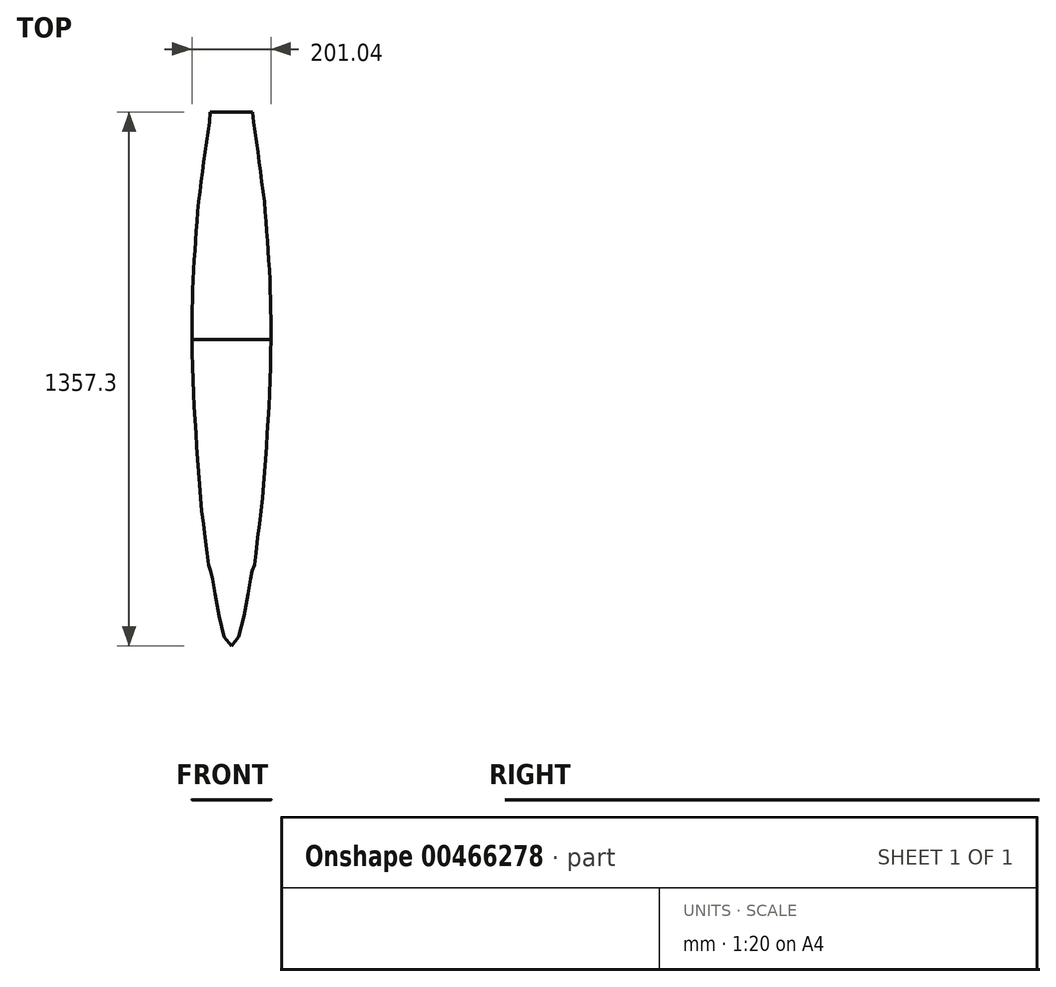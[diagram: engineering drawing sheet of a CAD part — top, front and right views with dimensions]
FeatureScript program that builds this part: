
annotation { "Feature Type Name" : "Feature", "Feature Type Description" : "" }
export const myFeature = defineFeature(function(context is Context, id is Id, definition is map)
    precondition{}
    {
        {
            var Q0;
            Q0=qCreatedBy(makeId("Front.planeOp"),FACE);
            cPlane(context, id + "F0", {"entities" : qUnion([Q0]), "cplaneType" : CPlaneType.OFFSET, "offset" : 76.2 * mm, "width" : 152.4 * mm, "height" : 152.4 * mm});
        }
        {
            var Q0;
            Q0=qCreatedBy(makeId("Front.planeOp"),FACE);
            cPlane(context, id + "F1", {"entities" : qUnion([Q0]), "cplaneType" : CPlaneType.OFFSET, "offset" : 149.22 * mm, "width" : 152.4 * mm, "height" : 152.4 * mm});
        }
        {
            var Q0;
            Q0=qCreatedBy(makeId("Front.planeOp"),FACE);
            cPlane(context, id + "F2", {"entities" : qUnion([Q0]), "cplaneType" : CPlaneType.OFFSET, "offset" : 223.85 * mm, "width" : 152.4 * mm, "height" : 152.4 * mm});
        }
        {
            var Q0;
            Q0=qCreatedBy(makeId("Front.planeOp"),FACE);
            cPlane(context, id + "F3", {"entities" : qUnion([Q0]), "cplaneType" : CPlaneType.OFFSET, "offset" : 296.88 * mm, "width" : 152.4 * mm, "height" : 152.4 * mm});
        }
        {
            var Q0;
            Q0=qCreatedBy(makeId("Front.planeOp"),FACE);
            cPlane(context, id + "F4", {"entities" : qUnion([Q0]), "cplaneType" : CPlaneType.OFFSET, "offset" : 371.47 * mm, "width" : 152.4 * mm, "height" : 152.4 * mm});
        }
        {
            var Q0;
            Q0=qCreatedBy(makeId("Front.planeOp"),FACE);
            cPlane(context, id + "F5", {"entities" : qUnion([Q0]), "cplaneType" : CPlaneType.OFFSET, "offset" : 444.5 * mm, "width" : 152.4 * mm, "height" : 152.4 * mm});
        }
        {
            var Q0;
            Q0=qCreatedBy(makeId("Front.planeOp"),FACE);
            cPlane(context, id + "F6", {"entities" : qUnion([Q0]), "cplaneType" : CPlaneType.OFFSET, "offset" : 517.52 * mm, "width" : 152.4 * mm, "height" : 152.4 * mm});
        }
        {
            var Q0;
            Q0=qCreatedBy(makeId("Front.planeOp"),FACE);
            cPlane(context, id + "F7", {"entities" : qUnion([Q0]), "cplaneType" : CPlaneType.OFFSET, "offset" : 590.55 * mm, "width" : 152.4 * mm, "height" : 152.4 * mm});
        }
        {
            var Q0;
            Q0=qCreatedBy(makeId("Front.planeOp"),FACE);
            cPlane(context, id + "F8", {"entities" : qUnion([Q0]), "cplaneType" : CPlaneType.OFFSET, "offset" : 658.83 * mm, "width" : 152.4 * mm, "height" : 152.4 * mm});
        }
        {
            var Q0;
            Q0=qCreatedBy(makeId("Front.planeOp"),FACE);
            cPlane(context, id + "F9", {"entities" : qUnion([Q0]), "cplaneType" : CPlaneType.OFFSET, "offset" : 730.25 * mm, "width" : 152.4 * mm, "height" : 152.4 * mm});
        }
        {
            var Q0;
            Q0=qCreatedBy(makeId("Front.planeOp"),FACE);
            cPlane(context, id + "F10", {"entities" : qUnion([Q0]), "cplaneType" : CPlaneType.OFFSET, "offset" : 801.7 * mm, "width" : 152.4 * mm, "height" : 152.4 * mm});
        }
        {
            var Q0;
            Q0=qCreatedBy(makeId("Front.planeOp"),FACE);
            cPlane(context, id + "F11", {"entities" : qUnion([Q0]), "cplaneType" : CPlaneType.OFFSET, "offset" : 874.73 * mm, "width" : 152.4 * mm, "height" : 152.4 * mm});
        }
        {
            var Q0;
            Q0=qCreatedBy(makeId("Front.planeOp"),FACE);
            cPlane(context, id + "F12", {"entities" : qUnion([Q0]), "cplaneType" : CPlaneType.OFFSET, "offset" : 949.32 * mm, "width" : 152.4 * mm, "height" : 152.4 * mm});
        }
        {
            var Q0;
            Q0=qCreatedBy(makeId("Front.planeOp"),FACE);
            cPlane(context, id + "F13", {"entities" : qUnion([Q0]), "cplaneType" : CPlaneType.OFFSET, "offset" : 1023.95 * mm, "width" : 152.4 * mm, "height" : 152.4 * mm});
        }
        {
            var Q0;
            Q0=qCreatedBy(makeId("Front.planeOp"),FACE);
            cPlane(context, id + "F14", {"entities" : qUnion([Q0]), "cplaneType" : CPlaneType.OFFSET, "offset" : 1096.98 * mm, "width" : 152.4 * mm, "height" : 152.4 * mm});
        }
        {
            var Q0;
            Q0=qCreatedBy(makeId("Front.planeOp"),FACE);
            cPlane(context, id + "F15", {"entities" : qUnion([Q0]), "cplaneType" : CPlaneType.OFFSET, "offset" : 1168.4 * mm, "width" : 152.4 * mm, "height" : 152.4 * mm});
        }
        {
            var Q0;
            Q0=qCreatedBy(makeId("Front.planeOp"),FACE);
            cPlane(context, id + "F16", {"entities" : qUnion([Q0]), "cplaneType" : CPlaneType.OFFSET, "offset" : 1233.5 * mm, "width" : 152.4 * mm, "height" : 152.4 * mm});
        }
        {
            var Q0;
            Q0=qCreatedBy(makeId("Front.planeOp"),FACE);
            cPlane(context, id + "F17", {"entities" : qUnion([Q0]), "cplaneType" : CPlaneType.OFFSET, "offset" : 1304.92 * mm, "width" : 152.4 * mm, "height" : 152.4 * mm});
        }
        {
            var Q0;
            Q0=qCreatedBy(makeId("Front.planeOp"),FACE);
            cPlane(context, id + "F18", {"entities" : qUnion([Q0]), "cplaneType" : CPlaneType.OFFSET, "offset" : 1377.95 * mm, "width" : 152.4 * mm, "height" : 152.4 * mm});
        }
        {
            var Q0;
            Q0=qCreatedBy(makeId("Front.planeOp"),FACE);
            cPlane(context, id + "F19", {"entities" : qUnion([Q0]), "cplaneType" : CPlaneType.OFFSET, "offset" : 1450.97 * mm, "width" : 152.4 * mm, "height" : 152.4 * mm});
        }
        {
            var Q0;
            Q0=qCreatedBy(makeId("Front.planeOp"),FACE);
            cPlane(context, id + "F20", {"entities" : qUnion([Q0]), "cplaneType" : CPlaneType.OFFSET, "offset" : 1524 * mm, "width" : 152.4 * mm, "height" : 152.4 * mm});
        }
        {
            var Q0;
            Q0=qCreatedBy(id+"F0.planeOp",FACE);
            var sketch = newSketch(context, id + "F21", { "sketchPlane" : qUnion([Q0])});
            skPoint(sketch, "E0", {"position": v(0, 45.6) * mm});
            skPoint(sketch, "E1", {"position": v(3.3, 99.95) * mm});
            skPoint(sketch, "E2", {"position": v(6.35, 110.5) * mm});
            skPoint(sketch, "E3", {"position": v(9.52, 114.5) * mm});
            skPoint(sketch, "E4", {"position": v(12.7, 116.71) * mm});
            skFitSpline(sketch, "E5", {"points": [v(12.7, 116.71) * mm, v(9.53, 114.5) * mm, v(6.35, 110.5) * mm, v(3.3, 99.95) * mm, v(0, 45.6) * mm], "startDerivative": vector(-25.87, -11.48) * mm, "endDerivative": vector(-23.07, -0.86) * mm});
            skFitSpline(sketch, "E6.MirrorCS", {"points": [v(-12.7, 116.71) * mm, v(-9.53, 114.5) * mm, v(-6.35, 110.5) * mm, v(-3.3, 99.95) * mm, v(0, 45.6) * mm], "startDerivative": vector(25.87, -11.48) * mm, "endDerivative": vector(23.07, -0.86) * mm});
            skSolve(sketch);
        }
        {
            var Q0;
            Q0=qCreatedBy(id+"F1.planeOp",FACE);
            var sketch = newSketch(context, id + "F22", { "sketchPlane" : qUnion([Q0])});
            skPoint(sketch, "E7", {"position": v(0, 3.56) * mm});
            skPoint(sketch, "E8", {"position": v(3.18, 4.45) * mm});
            skPoint(sketch, "E9", {"position": v(6.35, 14.99) * mm});
            skPoint(sketch, "E10", {"position": v(9.53, 28.96) * mm});
            skPoint(sketch, "E11", {"position": v(12.7, 55) * mm});
            skPoint(sketch, "E12", {"position": v(15.88, 72.77) * mm});
            skPoint(sketch, "E13", {"position": v(19.05, 83.06) * mm});
            skPoint(sketch, "E14", {"position": v(22.23, 92.58) * mm});
            skPoint(sketch, "E15", {"position": v(25.4, 99.7) * mm});
            skPoint(sketch, "E16", {"position": v(28.58, 105.16) * mm});
            skPoint(sketch, "E17", {"position": v(31.75, 109.7) * mm});
            skPoint(sketch, "E18", {"position": v(34.93, 114.43) * mm});
            skFitSpline(sketch, "E19", {"points": [v(34.93, 114.43) * mm, v(31.75, 109.7) * mm, v(28.58, 105.16) * mm, v(25.4, 99.7) * mm, v(22.23, 92.58) * mm, v(19.05, 83.06) * mm, v(15.88, 72.77) * mm, v(12.7, 55) * mm, v(9.53, 28.96) * mm, v(6.35, 14.99) * mm, v(3.18, 4.45) * mm, v(0, 3.56) * mm], "startDerivative": vector(-45.98, -69.77) * mm, "endDerivative": vector(-66.01, 0.7) * mm});
            skFitSpline(sketch, "E20.MirrorCS", {"points": [v(-34.93, 114.43) * mm, v(-31.75, 109.7) * mm, v(-28.58, 105.16) * mm, v(-25.4, 99.7) * mm, v(-22.23, 92.58) * mm, v(-19.05, 83.06) * mm, v(-15.88, 72.77) * mm, v(-12.7, 55) * mm, v(-9.53, 28.96) * mm, v(-6.35, 14.99) * mm, v(-3.18, 4.45) * mm, v(0, 3.56) * mm], "startDerivative": vector(45.98, -69.77) * mm, "endDerivative": vector(66.01, 0.7) * mm});
            skSolve(sketch);
        }
        {
            var Q0;
            Q0=qCreatedBy(id+"F2.planeOp",FACE);
            var sketch = newSketch(context, id + "F23", { "sketchPlane" : qUnion([Q0])});
            skPoint(sketch, "E21", {"position": v(0, 0) * mm});
            skPoint(sketch, "E22", {"position": v(3.18, 0.89) * mm});
            skPoint(sketch, "E23", {"position": v(6.35, 5.59) * mm});
            skPoint(sketch, "E24", {"position": v(9.53, 10.03) * mm});
            skPoint(sketch, "E25", {"position": v(12.7, 15.88) * mm});
            skPoint(sketch, "E26", {"position": v(15.88, 21.9) * mm});
            skPoint(sketch, "E27", {"position": v(19.05, 29.46) * mm});
            skPoint(sketch, "E28", {"position": v(22.23, 37.97) * mm});
            skPoint(sketch, "E29", {"position": v(25.4, 51.94) * mm});
            skPoint(sketch, "E30", {"position": v(28.58, 65.66) * mm});
            skPoint(sketch, "E31", {"position": v(31.75, 75.06) * mm});
            skPoint(sketch, "E32", {"position": v(34.93, 81.4) * mm});
            skPoint(sketch, "E33", {"position": v(38.1, 88.27) * mm});
            skPoint(sketch, "E34", {"position": v(41.28, 95.96) * mm});
            skPoint(sketch, "E35", {"position": v(44.45, 101.73) * mm});
            skPoint(sketch, "E36", {"position": v(47.63, 106.3) * mm});
            skPoint(sketch, "E37", {"position": v(50.8, 111.46) * mm});
            skFitSpline(sketch, "E38", {"points": [v(50.8, 111.46) * mm, v(47.63, 106.3) * mm, v(44.45, 101.73) * mm, v(41.28, 95.96) * mm, v(38.1, 88.27) * mm, v(34.93, 81.4) * mm, v(31.75, 75.06) * mm, v(28.58, 65.66) * mm, v(25.4, 51.94) * mm, v(22.23, 37.97) * mm, v(19.05, 29.46) * mm, v(15.88, 21.9) * mm, v(12.7, 15.88) * mm, v(9.53, 10.03) * mm, v(6.35, 5.59) * mm, v(3.18, 0.89) * mm, v(0, 0) * mm], "startDerivative": vector(-55.85, -94.62) * mm, "endDerivative": vector(-81.33, -5.78) * mm});
            skFitSpline(sketch, "E39.MirrorCS", {"points": [v(-50.8, 111.46) * mm, v(-47.63, 106.3) * mm, v(-44.45, 101.73) * mm, v(-41.28, 95.96) * mm, v(-38.1, 88.27) * mm, v(-34.93, 81.4) * mm, v(-31.75, 75.06) * mm, v(-28.58, 65.66) * mm, v(-25.4, 51.94) * mm, v(-22.23, 37.97) * mm, v(-19.05, 29.46) * mm, v(-15.88, 21.9) * mm, v(-12.7, 15.88) * mm, v(-9.53, 10.03) * mm, v(-6.35, 5.59) * mm, v(-3.18, 0.89) * mm, v(0, 0) * mm], "startDerivative": vector(55.85, -94.62) * mm, "endDerivative": vector(81.33, -5.78) * mm});
            skSolve(sketch);
        }
        {
            var Q0;
            Q0=qCreatedBy(id+"F3.planeOp",FACE);
            var sketch = newSketch(context, id + "F24", { "sketchPlane" : qUnion([Q0])});
            skPoint(sketch, "E40", {"position": v(0, 0) * mm});
            skPoint(sketch, "E41", {"position": v(3.18, 0) * mm});
            skPoint(sketch, "E42", {"position": v(6.35, 1.78) * mm});
            skPoint(sketch, "E43", {"position": v(9.53, 4.57) * mm});
            skPoint(sketch, "E44", {"position": v(12.7, 7.06) * mm});
            skPoint(sketch, "E45", {"position": v(15.88, 9.9) * mm});
            skPoint(sketch, "E46", {"position": v(19.05, 12.83) * mm});
            skPoint(sketch, "E47", {"position": v(22.23, 16.26) * mm});
            skPoint(sketch, "E48", {"position": v(25.4, 19.81) * mm});
            skPoint(sketch, "E49", {"position": v(28.58, 24.38) * mm});
            skPoint(sketch, "E50", {"position": v(31.75, 29.46) * mm});
            skPoint(sketch, "E51", {"position": v(34.93, 35.56) * mm});
            skPoint(sketch, "E52", {"position": v(38.1, 44.45) * mm});
            skPoint(sketch, "E53", {"position": v(41.28, 53.72) * mm});
            skPoint(sketch, "E54", {"position": v(44.45, 67.1) * mm});
            skPoint(sketch, "E55", {"position": v(47.63, 78.36) * mm});
            skPoint(sketch, "E56", {"position": v(50.8, 86.74) * mm});
            skPoint(sketch, "E57", {"position": v(52.07, 88.9) * mm});
            skPoint(sketch, "E58", {"position": v(53.98, 93.05) * mm});
            skFitSpline(sketch, "E59", {"points": [v(53.98, 93.05) * mm, v(52.07, 88.9) * mm, v(50.8, 86.74) * mm, v(47.63, 78.36) * mm, v(44.45, 67.1) * mm, v(41.28, 53.72) * mm, v(38.1, 44.45) * mm, v(34.93, 35.56) * mm, v(31.75, 29.46) * mm, v(28.58, 24.38) * mm, v(25.4, 19.81) * mm, v(22.23, 16.26) * mm, v(19.05, 12.83) * mm, v(15.88, 9.9) * mm, v(12.7, 7.06) * mm, v(9.53, 4.57) * mm, v(6.35, 1.78) * mm, v(3.18, 0) * mm, v(0, 0) * mm], "startDerivative": vector(0, -48.17) * mm, "endDerivative": vector(-83.73, 12.68) * mm});
            skFitSpline(sketch, "E60.MirrorCS", {"points": [v(-53.98, 93.05) * mm, v(-52.07, 88.9) * mm, v(-50.8, 86.74) * mm, v(-47.63, 78.36) * mm, v(-44.45, 67.1) * mm, v(-41.28, 53.72) * mm, v(-38.1, 44.45) * mm, v(-34.93, 35.56) * mm, v(-31.75, 29.46) * mm, v(-28.58, 24.38) * mm, v(-25.4, 19.81) * mm, v(-22.23, 16.26) * mm, v(-19.05, 12.83) * mm, v(-15.88, 9.9) * mm, v(-12.7, 7.06) * mm, v(-9.53, 4.57) * mm, v(-6.35, 1.78) * mm, v(-3.18, 0) * mm, v(0, 0) * mm], "startDerivative": vector(0, -48.17) * mm, "endDerivative": vector(83.73, 12.68) * mm});
            skSolve(sketch);
        }
        {
            var Q0;
            Q0=qCreatedBy(id+"F4.planeOp",FACE);
            var sketch = newSketch(context, id + "F25", { "sketchPlane" : qUnion([Q0])});
            skPoint(sketch, "E61", {"position": v(0, 0) * mm});
            skPoint(sketch, "E62", {"position": v(6.35, 1.52) * mm});
            skPoint(sketch, "E63", {"position": v(12.7, 3.3) * mm});
            skPoint(sketch, "E64", {"position": v(19.05, 6.22) * mm});
            skPoint(sketch, "E65", {"position": v(25.4, 9.14) * mm});
            skPoint(sketch, "E66", {"position": v(31.75, 13.46) * mm});
            skPoint(sketch, "E67", {"position": v(38.1, 18.16) * mm});
            skPoint(sketch, "E68", {"position": v(44.45, 25.27) * mm});
            skPoint(sketch, "E69", {"position": v(50.8, 35.05) * mm});
            skPoint(sketch, "E70", {"position": v(53.98, 40.39) * mm});
            skPoint(sketch, "E71", {"position": v(57.15, 48.26) * mm});
            skPoint(sketch, "E72", {"position": v(60.33, 58.42) * mm});
            skPoint(sketch, "E73", {"position": v(63.5, 72.64) * mm});
            skPoint(sketch, "E74", {"position": v(60.33, 74.42) * mm});
            skPoint(sketch, "E75", {"position": v(63.5, 93.22) * mm});
            skFitSpline(sketch, "E76", {"points": [v(63.5, 93.22) * mm, v(60.33, 74.42) * mm, v(63.5, 72.64) * mm, v(60.33, 58.42) * mm, v(57.15, 48.26) * mm, v(53.98, 40.39) * mm, v(50.8, 35.05) * mm, v(44.45, 25.27) * mm, v(38.1, 18.16) * mm, v(31.75, 13.46) * mm, v(25.4, 9.14) * mm, v(19.05, 6.22) * mm, v(12.7, 3.3) * mm, v(6.35, 1.52) * mm, v(0, 0) * mm], "startDerivative": vector(-79.19, -170.03) * mm, "endDerivative": vector(-100.93, -19.54) * mm});
            skFitSpline(sketch, "E77.MirrorCS", {"points": [v(-63.5, 93.22) * mm, v(-60.33, 74.42) * mm, v(-63.5, 72.64) * mm, v(-60.33, 58.42) * mm, v(-57.15, 48.26) * mm, v(-53.98, 40.39) * mm, v(-50.8, 35.05) * mm, v(-44.45, 25.27) * mm, v(-38.1, 18.16) * mm, v(-31.75, 13.46) * mm, v(-25.4, 9.14) * mm, v(-19.05, 6.22) * mm, v(-12.7, 3.3) * mm, v(-6.35, 1.52) * mm, v(0, 0) * mm], "startDerivative": vector(79.19, -170.03) * mm, "endDerivative": vector(100.93, -19.54) * mm});
            skSolve(sketch);
        }
        {
            var Q0;
            Q0=qCreatedBy(id+"F5.planeOp",FACE);
            var sketch = newSketch(context, id + "F26", { "sketchPlane" : qUnion([Q0])});
            skPoint(sketch, "E78", {"position": v(0, 0) * mm});
            skPoint(sketch, "E79", {"position": v(6.35, 1.27) * mm});
            skPoint(sketch, "E80", {"position": v(12.7, 2.03) * mm});
            skPoint(sketch, "E81", {"position": v(19.05, 3.81) * mm});
            skPoint(sketch, "E82", {"position": v(25.4, 4.83) * mm});
            skPoint(sketch, "E83", {"position": v(31.75, 6.48) * mm});
            skPoint(sketch, "E84", {"position": v(38.1, 7.87) * mm});
            skPoint(sketch, "E85", {"position": v(44.45, 9.65) * mm});
            skPoint(sketch, "E86", {"position": v(50.8, 12.45) * mm});
            skPoint(sketch, "E87", {"position": v(57.15, 17.27) * mm});
            skPoint(sketch, "E88", {"position": v(60.33, 21.2) * mm});
            skPoint(sketch, "E89", {"position": v(63.5, 25.4) * mm});
            skPoint(sketch, "E90", {"position": v(66.68, 30.86) * mm});
            skPoint(sketch, "E91", {"position": v(69.85, 37.85) * mm});
            skPoint(sketch, "E92", {"position": v(73.03, 47) * mm});
            skPoint(sketch, "E93", {"position": v(76.2, 60.05) * mm});
            skPoint(sketch, "E94", {"position": v(77.8, 71.88) * mm});
            skPoint(sketch, "E95", {"position": v(73.03, 73.91) * mm});
            skPoint(sketch, "E96", {"position": v(73.03, 93.22) * mm});
            skFitSpline(sketch, "E97", {"points": [v(73.03, 93.22) * mm, v(73.03, 73.91) * mm, v(77.8, 71.88) * mm, v(76.2, 60.05) * mm, v(73.03, 47) * mm, v(69.85, 37.85) * mm, v(66.68, 30.86) * mm, v(63.5, 25.4) * mm, v(60.33, 21.2) * mm, v(57.15, 17.27) * mm, v(50.8, 12.45) * mm, v(44.45, 9.65) * mm, v(38.1, 7.87) * mm, v(31.75, 6.48) * mm, v(25.4, 4.83) * mm, v(19.05, 3.81) * mm, v(12.7, 2.03) * mm, v(6.35, 1.27) * mm, v(0, 0) * mm], "startDerivative": vector(-44, -271.62) * mm, "endDerivative": vector(-123.94, -29.25) * mm});
            skFitSpline(sketch, "E98.MirrorCS", {"points": [v(-73.03, 93.22) * mm, v(-73.03, 73.91) * mm, v(-77.8, 71.88) * mm, v(-76.2, 60.05) * mm, v(-73.03, 47) * mm, v(-69.85, 37.85) * mm, v(-66.68, 30.86) * mm, v(-63.5, 25.4) * mm, v(-60.33, 21.2) * mm, v(-57.15, 17.27) * mm, v(-50.8, 12.45) * mm, v(-44.45, 9.65) * mm, v(-38.1, 7.87) * mm, v(-31.75, 6.48) * mm, v(-25.4, 4.83) * mm, v(-19.05, 3.81) * mm, v(-12.7, 2.03) * mm, v(-6.35, 1.27) * mm, v(0, 0) * mm], "startDerivative": vector(44, -271.62) * mm, "endDerivative": vector(123.94, -29.25) * mm});
            skSolve(sketch);
        }
        {
            var Q0;
            Q0=qCreatedBy(id+"F6.planeOp",FACE);
            var sketch = newSketch(context, id + "F27", { "sketchPlane" : qUnion([Q0])});
            skPoint(sketch, "E99", {"position": v(0, 0) * mm});
            skPoint(sketch, "E100", {"position": v(19.05, 0) * mm});
            skPoint(sketch, "E101", {"position": v(25.4, 0.5) * mm});
            skPoint(sketch, "E102", {"position": v(31.75, 1.27) * mm});
            skPoint(sketch, "E103", {"position": v(38.1, 2.29) * mm});
            skPoint(sketch, "E104", {"position": v(44.45, 3.3) * mm});
            skPoint(sketch, "E105", {"position": v(50.8, 4.57) * mm});
            skPoint(sketch, "E106", {"position": v(56.96, 6.48) * mm});
            skPoint(sketch, "E107", {"position": v(63.5, 8.64) * mm});
            skPoint(sketch, "E108", {"position": v(69.85, 11.43) * mm});
            skPoint(sketch, "E109", {"position": v(73.03, 14.22) * mm});
            skPoint(sketch, "E110", {"position": v(76.2, 18.29) * mm});
            skPoint(sketch, "E111", {"position": v(79.38, 22.86) * mm});
            skPoint(sketch, "E112", {"position": v(82.55, 29.21) * mm});
            skPoint(sketch, "E113", {"position": v(86.36, 47) * mm});
            skPoint(sketch, "E114", {"position": v(87.33, 72.14) * mm});
            skPoint(sketch, "E115", {"position": v(84.15, 74.68) * mm});
            skPoint(sketch, "E116", {"position": v(82.55, 93.22) * mm});
            skFitSpline(sketch, "E117", {"points": [v(82.55, 93.22) * mm, v(84.15, 74.68) * mm, v(87.33, 72.14) * mm, v(86.36, 47) * mm, v(82.55, 29.21) * mm, v(79.38, 22.86) * mm, v(76.2, 18.29) * mm, v(73.03, 14.22) * mm, v(69.85, 11.43) * mm, v(63.5, 8.64) * mm, v(56.96, 6.48) * mm, v(50.8, 4.57) * mm, v(44.45, 3.3) * mm, v(38.1, 2.29) * mm, v(31.75, 1.27) * mm, v(25.4, 0.5) * mm, v(19.05, 0) * mm, v(0, 0) * mm], "startDerivative": vector(-5.3, -256.42) * mm, "endDerivative": vector(-246.88, 8.43) * mm});
            skFitSpline(sketch, "E118.MirrorCS", {"points": [v(-82.55, 93.22) * mm, v(-84.15, 74.68) * mm, v(-87.33, 72.14) * mm, v(-86.36, 47) * mm, v(-82.55, 29.21) * mm, v(-79.38, 22.86) * mm, v(-76.2, 18.29) * mm, v(-73.03, 14.22) * mm, v(-69.85, 11.43) * mm, v(-63.5, 8.64) * mm, v(-56.96, 6.48) * mm, v(-50.8, 4.57) * mm, v(-44.45, 3.3) * mm, v(-38.1, 2.29) * mm, v(-31.75, 1.27) * mm, v(-25.4, 0.5) * mm, v(-19.05, 0) * mm, v(0, 0) * mm], "startDerivative": vector(5.3, -256.42) * mm, "endDerivative": vector(246.88, 8.43) * mm});
            skSolve(sketch);
        }
        {
            var Q0;
            Q0=qCreatedBy(id+"F7.planeOp",FACE);
            var sketch = newSketch(context, id + "F28", { "sketchPlane" : qUnion([Q0])});
            skPoint(sketch, "E119", {"position": v(31.75, 0) * mm});
            skPoint(sketch, "E120", {"position": v(38.1, 0.5) * mm});
            skPoint(sketch, "E121", {"position": v(44.45, 1.02) * mm});
            skPoint(sketch, "E122", {"position": v(50.8, 1.52) * mm});
            skPoint(sketch, "E123", {"position": v(57.15, 2.03) * mm});
            skPoint(sketch, "E124", {"position": v(63.5, 2.67) * mm});
            skPoint(sketch, "E125", {"position": v(69.85, 3.05) * mm});
            skPoint(sketch, "E126", {"position": v(76.2, 3.81) * mm});
            skPoint(sketch, "E127", {"position": v(79.38, 4.57) * mm});
            skPoint(sketch, "E128", {"position": v(82.55, 6.35) * mm});
            skPoint(sketch, "E129", {"position": v(85.73, 9.14) * mm});
            skPoint(sketch, "E130", {"position": v(88.9, 12.32) * mm});
            skPoint(sketch, "E131", {"position": v(92.08, 17.27) * mm});
            skPoint(sketch, "E132", {"position": v(95.25, 25.4) * mm});
            skPoint(sketch, "E133", {"position": v(96.85, 41.91) * mm});
            skPoint(sketch, "E134", {"position": v(95.25, 50.3) * mm});
            skPoint(sketch, "E135", {"position": v(95.25, 72.9) * mm});
            skPoint(sketch, "E136", {"position": v(90.5, 74.17) * mm});
            skPoint(sketch, "E137", {"position": v(88.9, 93.22) * mm});
            skFitSpline(sketch, "E138", {"points": [v(88.9, 93.22) * mm, v(90.5, 74.17) * mm, v(95.25, 72.9) * mm, v(95.25, 50.3) * mm, v(96.85, 41.91) * mm, v(95.25, 25.4) * mm, v(92.08, 17.27) * mm, v(88.9, 12.32) * mm, v(85.73, 9.14) * mm, v(82.55, 6.35) * mm, v(79.38, 4.57) * mm, v(76.2, 3.81) * mm, v(69.85, 3.05) * mm, v(63.5, 2.67) * mm, v(57.15, 2.03) * mm, v(50.8, 1.52) * mm, v(44.45, 1.02) * mm, v(38.1, 0.5) * mm, v(31.75, 0) * mm, v(0, 0) * mm], "startDerivative": vector(-17.9, -298.43) * mm, "endDerivative": vector(-369.3, 8.8) * mm});
            skFitSpline(sketch, "E139.MirrorCS", {"points": [v(-88.9, 93.22) * mm, v(-90.5, 74.17) * mm, v(-95.25, 72.9) * mm, v(-95.25, 50.3) * mm, v(-96.85, 41.91) * mm, v(-95.25, 25.4) * mm, v(-92.08, 17.27) * mm, v(-88.9, 12.32) * mm, v(-85.73, 9.14) * mm, v(-82.55, 6.35) * mm, v(-79.38, 4.57) * mm, v(-76.2, 3.81) * mm, v(-69.85, 3.05) * mm, v(-63.5, 2.67) * mm, v(-57.15, 2.03) * mm, v(-50.8, 1.52) * mm, v(-44.45, 1.02) * mm, v(-38.1, 0.5) * mm, v(-31.75, 0) * mm, v(0, 0) * mm], "startDerivative": vector(17.9, -298.43) * mm, "endDerivative": vector(369.3, 8.8) * mm});
            skSolve(sketch);
        }
        {
            var Q0;
            Q0=qCreatedBy(id+"F8.planeOp",FACE);
            var sketch = newSketch(context, id + "F29", { "sketchPlane" : qUnion([Q0])});
            skPoint(sketch, "E140", {"position": v(0, 0) * mm});
            skPoint(sketch, "E141", {"position": v(85.73, 0.5) * mm});
            skPoint(sketch, "E142", {"position": v(88.9, 1.27) * mm});
            skPoint(sketch, "E143", {"position": v(92.08, 3.05) * mm});
            skPoint(sketch, "E144", {"position": v(95.25, 5.59) * mm});
            skPoint(sketch, "E145", {"position": v(98.43, 9.4) * mm});
            skPoint(sketch, "E146", {"position": v(101.6, 15.5) * mm});
            skPoint(sketch, "E147", {"position": v(104.78, 27.94) * mm});
            skPoint(sketch, "E148", {"position": v(105.41, 41.15) * mm});
            skPoint(sketch, "E149", {"position": v(101.6, 49.02) * mm});
            skPoint(sketch, "E150", {"position": v(100.97, 72.14) * mm});
            skPoint(sketch, "E151", {"position": v(95.89, 73.91) * mm});
            skPoint(sketch, "E152", {"position": v(93.68, 93.22) * mm});
            skFitSpline(sketch, "E153", {"points": [v(93.68, 93.22) * mm, v(95.89, 73.91) * mm, v(100.97, 72.14) * mm, v(101.6, 49.02) * mm, v(105.41, 41.15) * mm, v(104.78, 27.94) * mm, v(101.6, 15.5) * mm, v(98.43, 9.4) * mm, v(95.25, 5.59) * mm, v(92.08, 3.05) * mm, v(88.9, 1.27) * mm, v(85.73, 0.5) * mm, v(0, 0) * mm], "startDerivative": vector(-5.44, -217.16) * mm, "endDerivative": vector(-515.09, 0) * mm});
            skFitSpline(sketch, "E154.MirrorCS", {"points": [v(-93.68, 93.22) * mm, v(-95.89, 73.91) * mm, v(-100.97, 72.14) * mm, v(-101.6, 49.02) * mm, v(-105.41, 41.15) * mm, v(-104.78, 27.94) * mm, v(-101.6, 15.5) * mm, v(-98.43, 9.4) * mm, v(-95.25, 5.59) * mm, v(-92.08, 3.05) * mm, v(-88.9, 1.27) * mm, v(-85.73, 0.5) * mm, v(0, 0) * mm], "startDerivative": vector(5.44, -217.16) * mm, "endDerivative": vector(515.09, 0) * mm});
            skSolve(sketch);
        }
        {
            var Q0;
            Q0=qCreatedBy(id+"F9.planeOp",FACE);
            var sketch = newSketch(context, id + "F30", { "sketchPlane" : qUnion([Q0])});
            skPoint(sketch, "E155", {"position": v(0, 0) * mm});
            skPoint(sketch, "E156", {"position": v(88.9, 0.5) * mm});
            skPoint(sketch, "E157", {"position": v(92.08, 0.76) * mm});
            skPoint(sketch, "E158", {"position": v(95.25, 1.27) * mm});
            skPoint(sketch, "E159", {"position": v(98.43, 2.29) * mm});
            skPoint(sketch, "E160", {"position": v(101.6, 4.45) * mm});
            skPoint(sketch, "E161", {"position": v(104.78, 7.37) * mm});
            skPoint(sketch, "E162", {"position": v(107.95, 12.95) * mm});
            skPoint(sketch, "E163", {"position": v(111.13, 25.4) * mm});
            skPoint(sketch, "E164", {"position": v(111.13, 41.15) * mm});
            skPoint(sketch, "E165", {"position": v(104.78, 50.04) * mm});
            skPoint(sketch, "E166", {"position": v(104.14, 71.63) * mm});
            skPoint(sketch, "E167", {"position": v(99.4, 73.66) * mm});
            skPoint(sketch, "E168", {"position": v(97.8, 93.22) * mm});
            skFitSpline(sketch, "E169", {"points": [v(97.8, 93.22) * mm, v(99.4, 73.66) * mm, v(104.14, 71.63) * mm, v(104.78, 50.04) * mm, v(111.13, 41.15) * mm, v(111.13, 25.4) * mm, v(107.95, 12.95) * mm, v(104.78, 7.37) * mm, v(101.6, 4.45) * mm, v(98.43, 2.29) * mm, v(95.25, 1.27) * mm, v(92.08, 0.76) * mm, v(88.9, 0.5) * mm, v(0, 0) * mm], "startDerivative": vector(-15.9, -223.3) * mm, "endDerivative": vector(-551.98, -1.2) * mm});
            skFitSpline(sketch, "E170.MirrorCS", {"points": [v(-97.8, 93.22) * mm, v(-99.4, 73.66) * mm, v(-104.14, 71.63) * mm, v(-104.78, 50.04) * mm, v(-111.13, 41.15) * mm, v(-111.13, 25.4) * mm, v(-107.95, 12.95) * mm, v(-104.78, 7.37) * mm, v(-101.6, 4.45) * mm, v(-98.43, 2.29) * mm, v(-95.25, 1.27) * mm, v(-92.08, 0.76) * mm, v(-88.9, 0.5) * mm, v(0, 0) * mm], "startDerivative": vector(15.9, -223.3) * mm, "endDerivative": vector(551.98, -1.2) * mm});
            skSolve(sketch);
        }
        {
            var Q0;
            Q0=qCreatedBy(id+"F10.planeOp",FACE);
            var sketch = newSketch(context, id + "F31", { "sketchPlane" : qUnion([Q0])});
            skPoint(sketch, "E171", {"position": v(0, 0) * mm});
            skPoint(sketch, "E172", {"position": v(101.6, 0.5) * mm});
            skPoint(sketch, "E173", {"position": v(104.78, 1.27) * mm});
            skPoint(sketch, "E174", {"position": v(107.95, 3.81) * mm});
            skPoint(sketch, "E175", {"position": v(111.13, 8.64) * mm});
            skPoint(sketch, "E176", {"position": v(114.8, 25.4) * mm});
            skPoint(sketch, "E177", {"position": v(114.3, 40.9) * mm});
            skPoint(sketch, "E178", {"position": v(107.95, 49.28) * mm});
            skPoint(sketch, "E179", {"position": v(106.38, 72.14) * mm});
            skPoint(sketch, "E180", {"position": v(101.6, 73.91) * mm});
            skPoint(sketch, "E181", {"position": v(99.82, 93.22) * mm});
            skFitSpline(sketch, "E182", {"points": [v(99.82, 93.22) * mm, v(101.6, 73.91) * mm, v(106.38, 72.14) * mm, v(107.95, 49.28) * mm, v(114.3, 40.9) * mm, v(114.8, 25.4) * mm, v(111.13, 8.64) * mm, v(107.95, 3.81) * mm, v(104.78, 1.27) * mm, v(101.6, 0.5) * mm, v(0, 0) * mm], "startDerivative": vector(-8.72, -198.23) * mm, "endDerivative": vector(-526.8, 1.1) * mm});
            skFitSpline(sketch, "E183.MirrorCS", {"points": [v(-99.82, 93.22) * mm, v(-101.6, 73.91) * mm, v(-106.38, 72.14) * mm, v(-107.95, 49.28) * mm, v(-114.3, 40.9) * mm, v(-114.8, 25.4) * mm, v(-111.13, 8.64) * mm, v(-107.95, 3.81) * mm, v(-104.78, 1.27) * mm, v(-101.6, 0.5) * mm, v(0, 0) * mm], "startDerivative": vector(8.72, -198.23) * mm, "endDerivative": vector(526.8, 1.1) * mm});
            skSolve(sketch);
        }
        {
            var Q0;
            Q0=qCreatedBy(id+"F12.planeOp",FACE);
            var sketch = newSketch(context, id + "F32", { "sketchPlane" : qUnion([Q0])});
            skPoint(sketch, "E184", {"position": v(0, 0) * mm});
            skPoint(sketch, "E185", {"position": v(88.9, 0.25) * mm});
            skPoint(sketch, "E186", {"position": v(92.08, 0.76) * mm});
            skPoint(sketch, "E187", {"position": v(95.25, 1.27) * mm});
            skPoint(sketch, "E188", {"position": v(98.43, 1.78) * mm});
            skPoint(sketch, "E189", {"position": v(101.6, 2.03) * mm});
            skPoint(sketch, "E190", {"position": v(104.78, 3.05) * mm});
            skPoint(sketch, "E191", {"position": v(107.95, 5.08) * mm});
            skPoint(sketch, "E192", {"position": v(111.13, 9.65) * mm});
            skPoint(sketch, "E193", {"position": v(114.3, 20.83) * mm});
            skPoint(sketch, "E194", {"position": v(114.3, 43.18) * mm});
            skPoint(sketch, "E195", {"position": v(106.38, 51.82) * mm});
            skPoint(sketch, "E196", {"position": v(104.78, 73.4) * mm});
            skPoint(sketch, "E197", {"position": v(101.6, 75.44) * mm});
            skPoint(sketch, "E198", {"position": v(98.43, 93.22) * mm});
            skFitSpline(sketch, "E199", {"points": [v(98.43, 93.22) * mm, v(101.6, 75.44) * mm, v(104.78, 73.4) * mm, v(106.38, 51.82) * mm, v(114.3, 43.18) * mm, v(114.3, 20.83) * mm, v(111.13, 9.65) * mm, v(107.95, 5.08) * mm, v(104.78, 3.05) * mm, v(101.6, 2.03) * mm, v(98.43, 1.78) * mm, v(95.25, 1.27) * mm, v(92.08, 0.76) * mm, v(88.9, 0.25) * mm, v(0, 0) * mm], "startDerivative": vector(17.96, -227.36) * mm, "endDerivative": vector(-573.99, 3.84) * mm});
            skFitSpline(sketch, "E200.MirrorCS", {"points": [v(-98.43, 93.22) * mm, v(-101.6, 75.44) * mm, v(-104.78, 73.4) * mm, v(-106.38, 51.82) * mm, v(-114.3, 43.18) * mm, v(-114.3, 20.83) * mm, v(-111.13, 9.65) * mm, v(-107.95, 5.08) * mm, v(-104.78, 3.05) * mm, v(-101.6, 2.03) * mm, v(-98.43, 1.78) * mm, v(-95.25, 1.27) * mm, v(-92.08, 0.76) * mm, v(-88.9, 0.25) * mm, v(0, 0) * mm], "startDerivative": vector(-17.96, -227.36) * mm, "endDerivative": vector(573.99, 3.84) * mm});
            skSolve(sketch);
        }
        {
            var Q0;
            Q0=qCreatedBy(id+"F13.planeOp",FACE);
            var sketch = newSketch(context, id + "F33", { "sketchPlane" : qUnion([Q0])});
            skPoint(sketch, "E201", {"position": v(0, 0) * mm});
            skPoint(sketch, "E202", {"position": v(88.9, 0.5) * mm});
            skPoint(sketch, "E203", {"position": v(92.08, 0.76) * mm});
            skPoint(sketch, "E204", {"position": v(95.25, 1.27) * mm});
            skPoint(sketch, "E205", {"position": v(98.43, 2.54) * mm});
            skPoint(sketch, "E206", {"position": v(101.6, 4.57) * mm});
            skPoint(sketch, "E207", {"position": v(104.78, 7.87) * mm});
            skPoint(sketch, "E208", {"position": v(107.95, 12.95) * mm});
            skPoint(sketch, "E209", {"position": v(111.13, 42.67) * mm});
            skPoint(sketch, "E210", {"position": v(103.5, 51.56) * mm});
            skPoint(sketch, "E211", {"position": v(101.6, 72.9) * mm});
            skPoint(sketch, "E212", {"position": v(98.43, 74.93) * mm});
            skPoint(sketch, "E213", {"position": v(96.22, 93.22) * mm});
            skFitSpline(sketch, "E214", {"points": [v(96.22, 93.22) * mm, v(98.43, 74.93) * mm, v(101.6, 72.9) * mm, v(103.5, 51.56) * mm, v(111.13, 42.67) * mm, v(107.95, 12.95) * mm, v(104.78, 7.87) * mm, v(101.6, 4.57) * mm, v(98.43, 2.54) * mm, v(95.25, 1.27) * mm, v(92.08, 0.76) * mm, v(88.9, 0.5) * mm, v(0, 0) * mm], "startDerivative": vector(2.85, -212.55) * mm, "endDerivative": vector(-519.16, -0.88) * mm});
            skFitSpline(sketch, "E215.MirrorCS", {"points": [v(-96.22, 93.22) * mm, v(-98.43, 74.93) * mm, v(-101.6, 72.9) * mm, v(-103.5, 51.56) * mm, v(-111.13, 42.67) * mm, v(-107.95, 12.95) * mm, v(-104.78, 7.87) * mm, v(-101.6, 4.57) * mm, v(-98.43, 2.54) * mm, v(-95.25, 1.27) * mm, v(-92.08, 0.76) * mm, v(-88.9, 0.5) * mm, v(0, 0) * mm], "startDerivative": vector(-2.85, -212.55) * mm, "endDerivative": vector(519.16, -0.88) * mm});
            skSolve(sketch);
        }
        {
            var Q0;
            Q0=qCreatedBy(id+"F14.planeOp",FACE);
            var sketch = newSketch(context, id + "F34", { "sketchPlane" : qUnion([Q0])});
            skPoint(sketch, "E216", {"position": v(0, 0) * mm});
            skPoint(sketch, "E217", {"position": v(85.73, 0.5) * mm});
            skPoint(sketch, "E218", {"position": v(88.9, 0.76) * mm});
            skPoint(sketch, "E219", {"position": v(92.08, 2.03) * mm});
            skPoint(sketch, "E220", {"position": v(95.25, 4.06) * mm});
            skPoint(sketch, "E221", {"position": v(98.43, 7.37) * mm});
            skPoint(sketch, "E222", {"position": v(101.6, 11.18) * mm});
            skPoint(sketch, "E223", {"position": v(104.78, 20.57) * mm});
            skPoint(sketch, "E224", {"position": v(105.74, 42.42) * mm});
            skPoint(sketch, "E225", {"position": v(99.4, 51.3) * mm});
            skPoint(sketch, "E226", {"position": v(98.43, 72.14) * mm});
            skPoint(sketch, "E227", {"position": v(93.04, 75.44) * mm});
            skPoint(sketch, "E228", {"position": v(91.44, 93.22) * mm});
            skFitSpline(sketch, "E229", {"points": [v(91.44, 93.22) * mm, v(93.04, 75.44) * mm, v(98.43, 72.14) * mm, v(99.4, 51.3) * mm, v(105.74, 42.42) * mm, v(104.78, 20.57) * mm, v(101.6, 11.18) * mm, v(98.43, 7.37) * mm, v(95.25, 4.06) * mm, v(92.08, 2.03) * mm, v(88.9, 0.76) * mm, v(85.73, 0.5) * mm, v(0, 0) * mm], "startDerivative": vector(-12.46, -204.91) * mm, "endDerivative": vector(-514.78, -2.97) * mm});
            skFitSpline(sketch, "E230.MirrorCS", {"points": [v(-91.44, 93.22) * mm, v(-93.04, 75.44) * mm, v(-98.43, 72.14) * mm, v(-99.4, 51.3) * mm, v(-105.74, 42.42) * mm, v(-104.78, 20.57) * mm, v(-101.6, 11.18) * mm, v(-98.43, 7.37) * mm, v(-95.25, 4.06) * mm, v(-92.08, 2.03) * mm, v(-88.9, 0.76) * mm, v(-85.73, 0.5) * mm, v(0, 0) * mm], "startDerivative": vector(12.46, -204.91) * mm, "endDerivative": vector(514.78, -2.97) * mm});
            skSolve(sketch);
        }
        {
            var Q0;
            Q0=qCreatedBy(id+"F15.planeOp",FACE);
            var sketch = newSketch(context, id + "F35", { "sketchPlane" : qUnion([Q0])});
            skPoint(sketch, "E231", {"position": v(0, 0) * mm});
            skPoint(sketch, "E232", {"position": v(73.03, 0.5) * mm});
            skPoint(sketch, "E233", {"position": v(76.2, 1.27) * mm});
            skPoint(sketch, "E234", {"position": v(82.55, 3.56) * mm});
            skPoint(sketch, "E235", {"position": v(85.73, 6.1) * mm});
            skPoint(sketch, "E236", {"position": v(88.9, 8.9) * mm});
            skPoint(sketch, "E237", {"position": v(92.08, 12.32) * mm});
            skPoint(sketch, "E238", {"position": v(95.25, 17.27) * mm});
            skPoint(sketch, "E239", {"position": v(98.43, 33.78) * mm});
            skPoint(sketch, "E240", {"position": v(98.76, 42.16) * mm});
            skPoint(sketch, "E241", {"position": v(92.08, 50.55) * mm});
            skPoint(sketch, "E242", {"position": v(92.08, 72.9) * mm});
            skPoint(sketch, "E243", {"position": v(88.9, 74.93) * mm});
            skPoint(sketch, "E244", {"position": v(87.33, 93.22) * mm});
            skFitSpline(sketch, "E245", {"points": [v(87.33, 93.22) * mm, v(88.9, 74.93) * mm, v(92.08, 72.9) * mm, v(92.08, 50.55) * mm, v(98.76, 42.16) * mm, v(98.43, 33.78) * mm, v(95.25, 17.27) * mm, v(92.08, 12.32) * mm, v(88.9, 8.9) * mm, v(85.73, 6.1) * mm, v(82.55, 3.56) * mm, v(76.2, 1.27) * mm, v(73.03, 0.5) * mm, v(0, 0) * mm], "startDerivative": vector(-7.98, -227.95) * mm, "endDerivative": vector(-489.86, 2.56) * mm});
            skFitSpline(sketch, "E246.MirrorCS", {"points": [v(-87.33, 93.22) * mm, v(-88.9, 74.93) * mm, v(-92.08, 72.9) * mm, v(-92.08, 50.55) * mm, v(-98.76, 42.16) * mm, v(-98.43, 33.78) * mm, v(-95.25, 17.27) * mm, v(-92.08, 12.32) * mm, v(-88.9, 8.9) * mm, v(-85.73, 6.1) * mm, v(-82.55, 3.56) * mm, v(-76.2, 1.27) * mm, v(-73.03, 0.5) * mm, v(0, 0) * mm], "startDerivative": vector(7.98, -227.95) * mm, "endDerivative": vector(489.86, 2.56) * mm});
            skSolve(sketch);
        }
        {
            var Q0;
            Q0=qCreatedBy(id+"F16.planeOp",FACE);
            var sketch = newSketch(context, id + "F36", { "sketchPlane" : qUnion([Q0])});
            skPoint(sketch, "E247", {"position": v(0, 0) * mm});
            skPoint(sketch, "E248", {"position": v(19.05, 0.5) * mm});
            skPoint(sketch, "E249", {"position": v(25.4, 1.02) * mm});
            skPoint(sketch, "E250", {"position": v(31.75, 1.52) * mm});
            skPoint(sketch, "E251", {"position": v(38.1, 2.03) * mm});
            skPoint(sketch, "E252", {"position": v(44.45, 2.54) * mm});
            skPoint(sketch, "E253", {"position": v(50.8, 2.8) * mm});
            skPoint(sketch, "E254", {"position": v(58.44, 4.32) * mm});
            skPoint(sketch, "E255", {"position": v(63.5, 6.1) * mm});
            skPoint(sketch, "E256", {"position": v(69.85, 9.9) * mm});
            skPoint(sketch, "E257", {"position": v(76.2, 14.48) * mm});
            skPoint(sketch, "E258", {"position": v(79.38, 17.78) * mm});
            skPoint(sketch, "E259", {"position": v(82.55, 21.59) * mm});
            skPoint(sketch, "E260", {"position": v(85.73, 28.96) * mm});
            skPoint(sketch, "E261", {"position": v(88.9, 42.67) * mm});
            skPoint(sketch, "E262", {"position": v(85.73, 50.8) * mm});
            skPoint(sketch, "E263", {"position": v(85.73, 73.66) * mm});
            skPoint(sketch, "E264", {"position": v(82.55, 74.68) * mm});
            skPoint(sketch, "E265", {"position": v(82.55, 93.22) * mm});
            skFitSpline(sketch, "E266", {"points": [v(82.55, 93.22) * mm, v(82.55, 74.68) * mm, v(85.73, 73.66) * mm, v(85.73, 50.8) * mm, v(88.9, 42.67) * mm, v(85.73, 28.96) * mm, v(82.55, 21.59) * mm, v(79.38, 17.78) * mm, v(76.2, 14.48) * mm, v(69.85, 9.9) * mm, v(63.5, 6.1) * mm, v(58.44, 4.32) * mm, v(50.8, 2.8) * mm, v(44.45, 2.54) * mm, v(38.1, 2.03) * mm, v(31.75, 1.52) * mm, v(25.4, 1.02) * mm, v(19.05, 0.5) * mm, v(0, 0) * mm], "startDerivative": vector(-38.9, -299.85) * mm, "endDerivative": vector(-260.37, -2.96) * mm});
            skFitSpline(sketch, "E267.MirrorCS", {"points": [v(-82.55, 93.22) * mm, v(-82.55, 74.68) * mm, v(-85.73, 73.66) * mm, v(-85.73, 50.8) * mm, v(-88.9, 42.67) * mm, v(-85.73, 28.96) * mm, v(-82.55, 21.59) * mm, v(-79.38, 17.78) * mm, v(-76.2, 14.48) * mm, v(-69.85, 9.9) * mm, v(-63.5, 6.1) * mm, v(-58.44, 4.32) * mm, v(-50.8, 2.8) * mm, v(-44.45, 2.54) * mm, v(-38.1, 2.03) * mm, v(-31.75, 1.52) * mm, v(-25.4, 1.02) * mm, v(-19.05, 0.5) * mm, v(0, 0) * mm], "startDerivative": vector(38.9, -299.85) * mm, "endDerivative": vector(260.37, -2.96) * mm});
            skSolve(sketch);
        }
        {
            var Q0;
            Q0=qCreatedBy(id+"F17.planeOp",FACE);
            var sketch = newSketch(context, id + "F37", { "sketchPlane" : qUnion([Q0])});
            skPoint(sketch, "E268", {"position": v(0, 0) * mm});
            skPoint(sketch, "E269", {"position": v(12.7, 2.03) * mm});
            skPoint(sketch, "E270", {"position": v(19.05, 5.59) * mm});
            skPoint(sketch, "E271", {"position": v(25.4, 7.37) * mm});
            skPoint(sketch, "E272", {"position": v(31.75, 8.64) * mm});
            skPoint(sketch, "E273", {"position": v(38.1, 9.14) * mm});
            skPoint(sketch, "E274", {"position": v(44.45, 10.92) * mm});
            skPoint(sketch, "E275", {"position": v(50.8, 13.72) * mm});
            skPoint(sketch, "E276", {"position": v(57.15, 17.78) * mm});
            skPoint(sketch, "E277", {"position": v(63.5, 22.86) * mm});
            skPoint(sketch, "E278", {"position": v(69.85, 29.72) * mm});
            skPoint(sketch, "E279", {"position": v(76.2, 45.72) * mm});
            skPoint(sketch, "E280", {"position": v(79.38, 73.15) * mm});
            skPoint(sketch, "E281", {"position": v(76.2, 74.42) * mm});
            skPoint(sketch, "E282", {"position": v(76.2, 93.22) * mm});
            skFitSpline(sketch, "E283", {"points": [v(76.2, 93.22) * mm, v(76.2, 74.42) * mm, v(79.38, 73.15) * mm, v(76.2, 45.72) * mm, v(69.85, 29.72) * mm, v(63.5, 22.86) * mm, v(57.15, 17.78) * mm, v(50.8, 13.72) * mm, v(44.45, 10.92) * mm, v(38.1, 9.14) * mm, v(31.75, 8.64) * mm, v(25.4, 7.37) * mm, v(19.05, 5.59) * mm, v(12.7, 2.03) * mm, v(0, 0) * mm], "startDerivative": vector(-31.4, -253.95) * mm, "endDerivative": vector(-171.34, 3.26) * mm});
            skFitSpline(sketch, "E284.MirrorCS", {"points": [v(-76.2, 93.22) * mm, v(-76.2, 74.42) * mm, v(-79.38, 73.15) * mm, v(-76.2, 45.72) * mm, v(-69.85, 29.72) * mm, v(-63.5, 22.86) * mm, v(-57.15, 17.78) * mm, v(-50.8, 13.72) * mm, v(-44.45, 10.92) * mm, v(-38.1, 9.14) * mm, v(-31.75, 8.64) * mm, v(-25.4, 7.37) * mm, v(-19.05, 5.59) * mm, v(-12.7, 2.03) * mm, v(0, 0) * mm], "startDerivative": vector(31.4, -253.95) * mm, "endDerivative": vector(171.34, 3.26) * mm});
            skSolve(sketch);
        }
        {
            var Q0;
            Q0=qCreatedBy(id+"F18.planeOp",FACE);
            var sketch = newSketch(context, id + "F38", { "sketchPlane" : qUnion([Q0])});
            skPoint(sketch, "E285", {"position": v(0, 0) * mm});
            skPoint(sketch, "E286", {"position": v(6.35, 4.32) * mm});
            skPoint(sketch, "E287", {"position": v(12.7, 11.94) * mm});
            skPoint(sketch, "E288", {"position": v(19.05, 15.5) * mm});
            skPoint(sketch, "E289", {"position": v(25.4, 18.29) * mm});
            skPoint(sketch, "E290", {"position": v(31.75, 20.32) * mm});
            skPoint(sketch, "E291", {"position": v(38.1, 22.35) * mm});
            skPoint(sketch, "E292", {"position": v(44.45, 25.9) * mm});
            skPoint(sketch, "E293", {"position": v(50.8, 30.73) * mm});
            skPoint(sketch, "E294", {"position": v(57.15, 36.32) * mm});
            skPoint(sketch, "E295", {"position": v(63.5, 48.51) * mm});
            skPoint(sketch, "E296", {"position": v(66.68, 57.91) * mm});
            skPoint(sketch, "E297", {"position": v(69.85, 72.9) * mm});
            skPoint(sketch, "E298", {"position": v(66.68, 74.42) * mm});
            skPoint(sketch, "E299", {"position": v(66.68, 93.22) * mm});
            skFitSpline(sketch, "E300", {"points": [v(66.68, 93.22) * mm, v(66.68, 74.42) * mm, v(69.85, 72.9) * mm, v(66.68, 57.91) * mm, v(63.5, 48.51) * mm, v(57.15, 36.32) * mm, v(50.8, 30.73) * mm, v(44.45, 25.9) * mm, v(38.1, 22.35) * mm, v(31.75, 20.32) * mm, v(25.4, 18.29) * mm, v(19.05, 15.5) * mm, v(12.7, 11.94) * mm, v(6.35, 4.32) * mm, v(0, 0) * mm], "startDerivative": vector(-32.12, -243.34) * mm, "endDerivative": vector(-111.57, 0) * mm});
            skFitSpline(sketch, "E301.MirrorCS", {"points": [v(-66.68, 93.22) * mm, v(-66.68, 74.42) * mm, v(-69.85, 72.9) * mm, v(-66.68, 57.91) * mm, v(-63.5, 48.51) * mm, v(-57.15, 36.32) * mm, v(-50.8, 30.73) * mm, v(-44.45, 25.9) * mm, v(-38.1, 22.35) * mm, v(-31.75, 20.32) * mm, v(-25.4, 18.29) * mm, v(-19.05, 15.5) * mm, v(-12.7, 11.94) * mm, v(-6.35, 4.32) * mm, v(0, 0) * mm], "startDerivative": vector(32.12, -243.34) * mm, "endDerivative": vector(111.57, 0) * mm});
            skSolve(sketch);
        }
        {
            var Q0;
            Q0=qCreatedBy(makeId("Right.planeOp"),FACE);
            var sketch = newSketch(context, id + "F39", { "sketchPlane" : qUnion([Q0])});
            skPoint(sketch, "E302", {"position": v(-200.03, 0) * mm});
            skPoint(sketch, "E303", {"position": v(-174.63, 0.5) * mm});
            skPoint(sketch, "E304", {"position": v(-136.53, 4.32) * mm});
            skPoint(sketch, "E305", {"position": v(-130.18, 6.1) * mm});
            skPoint(sketch, "E306", {"position": v(-123.83, 7.11) * mm});
            skPoint(sketch, "E307", {"position": v(-117.48, 8.38) * mm});
            skPoint(sketch, "E308", {"position": v(-111.13, 9.78) * mm});
            skPoint(sketch, "E309", {"position": v(-104.78, 11.68) * mm});
            skPoint(sketch, "E310", {"position": v(-98.43, 14.48) * mm});
            skPoint(sketch, "E311", {"position": v(-92.08, 19.05) * mm});
            skPoint(sketch, "E312", {"position": v(-85.73, 25.02) * mm});
            skPoint(sketch, "E313", {"position": v(-79.38, 34.42) * mm});
            skPoint(sketch, "E314", {"position": v(-75.57, 57.15) * mm});
            skPoint(sketch, "E315", {"position": v(-74.93, 72.9) * mm});
            skPoint(sketch, "E316", {"position": v(-73.03, 89.66) * mm});
            skPoint(sketch, "E317", {"position": v(-69.85, 101.47) * mm});
            skPoint(sketch, "E318", {"position": v(-66.68, 108.59) * mm});
            skPoint(sketch, "E319", {"position": v(-63.5, 112.27) * mm});
            skPoint(sketch, "E320", {"position": v(-60.33, 116.84) * mm});
            skPoint(sketch, "E321", {"position": v(-76.2, 45.6) * mm});
            skPoint(sketch, "E322", {"position": v(-149.23, 3.56) * mm});
            skPoint(sketch, "E323", {"position": v(-1457.33, 9.9) * mm});
            skPoint(sketch, "E324", {"position": v(-1450.98, 0) * mm});
            skPoint(sketch, "E325", {"position": v(-1463.67, 16.51) * mm});
            skPoint(sketch, "E326", {"position": v(-1470.03, 16.51) * mm});
            skPoint(sketch, "E327", {"position": v(-1476.38, 16.51) * mm});
            skPoint(sketch, "E328", {"position": v(-1482.73, 16.51) * mm});
            skPoint(sketch, "E329", {"position": v(-1489.08, 22.86) * mm});
            skPoint(sketch, "E330", {"position": v(-1495.43, 26.29) * mm});
            skPoint(sketch, "E331", {"position": v(-1501.78, 28.57) * mm});
            skPoint(sketch, "E332", {"position": v(-1508.13, 29.97) * mm});
            skPoint(sketch, "E333", {"position": v(-1514.47, 30.73) * mm});
            skPoint(sketch, "E334", {"position": v(-1520.83, 30.73) * mm});
            skPoint(sketch, "E335", {"position": v(-1527.18, 30.73) * mm});
            skPoint(sketch, "E336", {"position": v(-1533.53, 30.73) * mm});
            skPoint(sketch, "E337", {"position": v(-1539.88, 31.24) * mm});
            skPoint(sketch, "E338", {"position": v(-1546.23, 31.5) * mm});
            skPoint(sketch, "E339", {"position": v(-1552.58, 31.75) * mm});
            skPoint(sketch, "E340", {"position": v(-1558.93, 31.88) * mm});
            skPoint(sketch, "E341", {"position": v(-1565.28, 32) * mm});
            skPoint(sketch, "E342", {"position": v(-1571.62, 32.51) * mm});
            skPoint(sketch, "E343", {"position": v(-1577.98, 33.27) * mm});
            skPoint(sketch, "E344", {"position": v(-1584.33, 34.29) * mm});
            skPoint(sketch, "E345", {"position": v(-1590.67, 35.3) * mm});
            skPoint(sketch, "E346", {"position": v(-1597.03, 36.32) * mm});
            skPoint(sketch, "E347", {"position": v(-1603.38, 37.34) * mm});
            skPoint(sketch, "E348", {"position": v(-1609.73, 38.6) * mm});
            skPoint(sketch, "E349", {"position": v(-1616.08, 40.13) * mm});
            skPoint(sketch, "E350", {"position": v(-1622.43, 41.27) * mm});
            skPoint(sketch, "E351", {"position": v(-1628.78, 42.67) * mm});
            skPoint(sketch, "E352", {"position": v(-1635.13, 44.07) * mm});
            skPoint(sketch, "E353", {"position": v(-1641.48, 45.72) * mm});
            skPoint(sketch, "E354", {"position": v(-1647.83, 47.62) * mm});
            skPoint(sketch, "E355", {"position": v(-1654.18, 50.04) * mm});
            skPoint(sketch, "E356", {"position": v(-1657.35, 51.18) * mm});
            skPoint(sketch, "E357", {"position": v(-1660.53, 52.58) * mm});
            skPoint(sketch, "E358", {"position": v(-1663.7, 56.51) * mm});
            skPoint(sketch, "E359", {"position": v(-1664.34, 63.25) * mm});
            skPoint(sketch, "E360", {"position": v(-1663.7, 69.6) * mm});
            skPoint(sketch, "E361", {"position": v(-1662.3, 76.2) * mm});
            skPoint(sketch, "E362", {"position": v(-1660.53, 82.3) * mm});
            skPoint(sketch, "E363", {"position": v(-1657.35, 87.63) * mm});
            skPoint(sketch, "E364", {"position": v(-1654.18, 93.22) * mm});
            skPoint(sketch, "E365", {"position": v(-1377.95, 0) * mm});
            skPoint(sketch, "E366", {"position": v(-1304.93, 0) * mm});
            skPoint(sketch, "E367", {"position": v(-1233.5, 0) * mm});
            skPoint(sketch, "E368", {"position": v(-1168.4, 0) * mm});
            skPoint(sketch, "E369", {"position": v(-1096.98, 0) * mm});
            skPoint(sketch, "E370", {"position": v(-1023.95, 0) * mm});
            skPoint(sketch, "E371", {"position": v(-949.33, 0) * mm});
            skPoint(sketch, "E372", {"position": v(-801.7, 0) * mm});
            skPoint(sketch, "E373", {"position": v(-730.25, 0) * mm});
            skPoint(sketch, "E374", {"position": v(-658.83, 0) * mm});
            skPoint(sketch, "E375", {"position": v(-590.55, 0) * mm});
            skPoint(sketch, "E376", {"position": v(-517.52, 0) * mm});
            skPoint(sketch, "E377", {"position": v(-444.5, 0) * mm});
            skPoint(sketch, "E378", {"position": v(-371.48, 0) * mm});
            skPoint(sketch, "E379", {"position": v(-296.88, 0) * mm});
            skPoint(sketch, "E380", {"position": v(-223.85, 0) * mm});
            skFitSpline(sketch, "E381", {"points": [v(-60.33, 116.84) * mm, v(-63.5, 112.27) * mm, v(-66.68, 108.59) * mm, v(-69.85, 101.47) * mm, v(-73.03, 89.66) * mm, v(-74.93, 72.9) * mm, v(-75.57, 57.15) * mm, v(-76.2, 45.6) * mm, v(-79.38, 34.42) * mm, v(-85.73, 25.02) * mm, v(-92.08, 19.05) * mm, v(-98.43, 14.48) * mm, v(-104.78, 11.68) * mm, v(-111.13, 9.78) * mm, v(-117.48, 8.38) * mm, v(-123.83, 7.11) * mm, v(-130.18, 6.1) * mm, v(-136.53, 4.32) * mm, v(-149.23, 3.56) * mm, v(-174.63, 0.5) * mm, v(-200.03, 0) * mm, v(-223.85, 0) * mm, v(-296.88, 0) * mm], "startDerivative": vector(-100.83, -159.31) * mm, "endDerivative": vector(-744.4, 19.3) * mm});
            skPoint(sketch, "E382", {"position": v(-1438.28, 0) * mm});
            skFitSpline(sketch, "E383", {"points": [v(-1654.18, 93.22) * mm, v(-1657.35, 87.63) * mm, v(-1660.53, 82.3) * mm, v(-1662.3, 76.2) * mm, v(-1663.7, 69.6) * mm, v(-1664.34, 63.25) * mm, v(-1663.7, 56.51) * mm, v(-1660.53, 52.58) * mm, v(-1657.35, 51.18) * mm, v(-1654.18, 50.04) * mm, v(-1647.83, 47.62) * mm, v(-1641.48, 45.72) * mm, v(-1635.13, 44.07) * mm, v(-1628.78, 42.67) * mm, v(-1622.43, 41.27) * mm, v(-1616.08, 40.13) * mm, v(-1609.73, 38.6) * mm, v(-1603.38, 37.34) * mm, v(-1597.03, 36.32) * mm, v(-1590.67, 35.3) * mm, v(-1584.33, 34.29) * mm, v(-1577.98, 33.27) * mm, v(-1571.62, 32.51) * mm, v(-1565.28, 32) * mm, v(-1558.93, 31.88) * mm, v(-1552.58, 31.75) * mm, v(-1546.23, 31.5) * mm, v(-1539.88, 31.24) * mm, v(-1533.53, 30.73) * mm, v(-1527.18, 30.73) * mm, v(-1520.83, 30.73) * mm, v(-1514.47, 30.73) * mm, v(-1508.13, 29.97) * mm, v(-1501.78, 28.57) * mm, v(-1495.43, 26.29) * mm, v(-1489.08, 22.86) * mm, v(-1482.73, 16.51) * mm, v(-1476.38, 16.51) * mm, v(-1470.03, 16.51) * mm, v(-1463.67, 16.51) * mm, v(-1457.33, 9.9) * mm, v(-1450.98, 0) * mm], "startDerivative": vector(-114.87, -270) * mm, "endDerivative": vector(190.57, -304.77) * mm});
            skFitSpline(sketch, "E384", {"points": [v(-1450.98, 0) * mm, v(-1377.95, 0) * mm, v(-1304.93, 0) * mm, v(-1233.5, 0) * mm, v(-1168.4, 0) * mm, v(-1096.98, 0) * mm, v(-1023.95, 0) * mm, v(-949.33, 0) * mm, v(-801.7, 0) * mm, v(-730.25, 0) * mm, v(-658.83, 0) * mm, v(-590.55, 0) * mm, v(-517.52, 0) * mm, v(-444.5, 0) * mm, v(-371.48, 0) * mm, v(-296.88, 0) * mm], "startDerivative": vector(1118.36, 0) * mm, "endDerivative": vector(1133, 0) * mm});
            skSolve(sketch);
        }
        {
            var Q0;
            Q0=qCreatedBy(id+"F19.planeOp",FACE);
            var sketch = newSketch(context, id + "F40", { "sketchPlane" : qUnion([Q0])});
            skPoint(sketch, "E385", {"position": v(0, 0) * mm});
            skPoint(sketch, "E386", {"position": v(3.18, 7.62) * mm});
            skPoint(sketch, "E387", {"position": v(6.35, 16) * mm});
            skPoint(sketch, "E388", {"position": v(9.53, 20.32) * mm});
            skPoint(sketch, "E389", {"position": v(12.7, 23.62) * mm});
            skPoint(sketch, "E390", {"position": v(15.8, 25.65) * mm});
            skPoint(sketch, "E391", {"position": v(19.05, 27.43) * mm});
            skPoint(sketch, "E392", {"position": v(22.23, 29.97) * mm});
            skPoint(sketch, "E393", {"position": v(25.4, 31.37) * mm});
            skPoint(sketch, "E394", {"position": v(28.58, 33.27) * mm});
            skPoint(sketch, "E395", {"position": v(31.75, 34.67) * mm});
            skPoint(sketch, "E396", {"position": v(34.93, 36.07) * mm});
            skPoint(sketch, "E397", {"position": v(38.1, 37.6) * mm});
            skPoint(sketch, "E398", {"position": v(41.28, 39.37) * mm});
            skPoint(sketch, "E399", {"position": v(44.45, 42.3) * mm});
            skPoint(sketch, "E400", {"position": v(47.63, 46.23) * mm});
            skPoint(sketch, "E401", {"position": v(50.8, 53.98) * mm});
            skPoint(sketch, "E402", {"position": v(53.97, 66.3) * mm});
            skPoint(sketch, "E403", {"position": v(57.15, 93.22) * mm});
            skFitSpline(sketch, "E404", {"points": [v(57.15, 93.22) * mm, v(53.97, 66.3) * mm, v(50.8, 53.98) * mm, v(47.63, 46.23) * mm, v(44.45, 42.3) * mm, v(41.28, 39.37) * mm, v(38.1, 37.6) * mm, v(34.93, 36.07) * mm, v(31.75, 34.67) * mm, v(28.58, 33.27) * mm, v(25.4, 31.37) * mm, v(22.23, 29.97) * mm, v(19.05, 27.43) * mm, v(15.8, 25.65) * mm, v(12.7, 23.62) * mm, v(9.53, 20.32) * mm, v(6.35, 16) * mm, v(3.18, 7.62) * mm, v(0, 0) * mm], "startDerivative": vector(-22.38, -254.43) * mm, "endDerivative": vector(-118.76, 14.68) * mm});
            skFitSpline(sketch, "E405.MirrorCS", {"points": [v(-57.15, 93.22) * mm, v(-53.97, 66.3) * mm, v(-50.8, 53.98) * mm, v(-47.63, 46.23) * mm, v(-44.45, 42.3) * mm, v(-41.28, 39.37) * mm, v(-38.1, 37.6) * mm, v(-34.93, 36.07) * mm, v(-31.75, 34.67) * mm, v(-28.58, 33.27) * mm, v(-25.4, 31.37) * mm, v(-22.23, 29.97) * mm, v(-19.05, 27.43) * mm, v(-15.8, 25.65) * mm, v(-12.7, 23.62) * mm, v(-9.53, 20.32) * mm, v(-6.35, 16) * mm, v(-3.18, 7.62) * mm, v(0, 0) * mm], "startDerivative": vector(22.38, -254.43) * mm, "endDerivative": vector(118.76, 14.68) * mm});
            skSolve(sketch);
        }
        {
            var Q0;
            Q0=qCreatedBy(id+"F20.planeOp",FACE);
            var sketch = newSketch(context, id + "F41", { "sketchPlane" : qUnion([Q0])});
            skPoint(sketch, "E406", {"position": v(0, 30.73) * mm});
            skPoint(sketch, "E407", {"position": v(6.35, 31.5) * mm});
            skPoint(sketch, "E408", {"position": v(12.7, 33.53) * mm});
            skPoint(sketch, "E409", {"position": v(19.05, 37.6) * mm});
            skPoint(sketch, "E410", {"position": v(22.86, 41.91) * mm});
            skPoint(sketch, "E411", {"position": v(25.9, 46.74) * mm});
            skPoint(sketch, "E412", {"position": v(29.21, 52.32) * mm});
            skPoint(sketch, "E413", {"position": v(31.75, 57.91) * mm});
            skPoint(sketch, "E414", {"position": v(34.93, 67.06) * mm});
            skPoint(sketch, "E415", {"position": v(38.1, 77.72) * mm});
            skPoint(sketch, "E416", {"position": v(41.28, 93.22) * mm});
            skFitSpline(sketch, "E417", {"points": [v(41.28, 93.22) * mm, v(38.1, 77.72) * mm, v(34.93, 67.06) * mm, v(31.75, 57.91) * mm, v(29.21, 52.32) * mm, v(25.9, 46.74) * mm, v(22.86, 41.91) * mm, v(19.05, 37.6) * mm, v(12.7, 33.53) * mm, v(6.35, 31.5) * mm, v(0, 30.73) * mm], "startDerivative": vector(-19.91, -124.96) * mm, "endDerivative": vector(-72.06, -7.83) * mm});
            skFitSpline(sketch, "E418.MirrorCS", {"points": [v(-41.28, 93.22) * mm, v(-38.1, 77.72) * mm, v(-34.93, 67.06) * mm, v(-31.75, 57.91) * mm, v(-29.21, 52.32) * mm, v(-25.9, 46.74) * mm, v(-22.86, 41.91) * mm, v(-19.05, 37.6) * mm, v(-12.7, 33.53) * mm, v(-6.35, 31.5) * mm, v(0, 30.73) * mm], "startDerivative": vector(19.91, -124.96) * mm, "endDerivative": vector(72.06, -7.83) * mm});
            skSolve(sketch);
        }
        {
            var Q0;
            Q0=qCreatedBy(id+"F11.planeOp",FACE);
            var sketch = newSketch(context, id + "F42", { "sketchPlane" : qUnion([Q0])});
            skPoint(sketch, "E419", {"position": v(0, 0) * mm});
            skPoint(sketch, "E420", {"position": v(101.6, 0.5) * mm});
            skPoint(sketch, "E421", {"position": v(104.78, 1.27) * mm});
            skPoint(sketch, "E422", {"position": v(107.95, 3.81) * mm});
            skPoint(sketch, "E423", {"position": v(111.13, 8.64) * mm});
            skPoint(sketch, "E424", {"position": v(114.8, 25.4) * mm});
            skPoint(sketch, "E425", {"position": v(114.3, 40.9) * mm});
            skPoint(sketch, "E426", {"position": v(107.95, 49.28) * mm});
            skPoint(sketch, "E427", {"position": v(106.38, 72.14) * mm});
            skPoint(sketch, "E428", {"position": v(101.6, 73.91) * mm});
            skPoint(sketch, "E429", {"position": v(99.82, 93.22) * mm});
            skFitSpline(sketch, "E430", {"points": [v(99.82, 93.22) * mm, v(101.6, 73.91) * mm, v(106.38, 72.14) * mm, v(107.95, 49.28) * mm, v(114.3, 40.9) * mm, v(114.8, 25.4) * mm, v(111.13, 8.64) * mm, v(107.95, 3.81) * mm, v(104.78, 1.27) * mm, v(101.6, 0.5) * mm, v(0, 0) * mm], "startDerivative": vector(-8.72, -198.23) * mm, "endDerivative": vector(-526.8, 1.1) * mm});
            skFitSpline(sketch, "E431.MirrorCS", {"points": [v(-99.82, 93.22) * mm, v(-101.6, 73.91) * mm, v(-106.38, 72.14) * mm, v(-107.95, 49.28) * mm, v(-114.3, 40.9) * mm, v(-114.8, 25.4) * mm, v(-111.13, 8.64) * mm, v(-107.95, 3.81) * mm, v(-104.78, 1.27) * mm, v(-101.6, 0.5) * mm, v(0, 0) * mm], "startDerivative": vector(8.72, -198.23) * mm, "endDerivative": vector(526.8, 1.1) * mm});
            skSolve(sketch);
        }
        {
            var Q0;
            Q0=qCreatedBy(makeId("Front.planeOp"),FACE);
            cPlane(context, id + "F43", {"entities" : qUnion([Q0]), "cplaneType" : CPlaneType.OFFSET, "offset" : 1463.67 * mm, "width" : 152.4 * mm, "height" : 152.4 * mm});
        }
        {
            var Q0;
            Q0=qCreatedBy(id+"F43.planeOp",FACE);
            var sketch = newSketch(context, id + "F44", { "sketchPlane" : qUnion([Q0])});
            skPoint(sketch, "E432", {"position": v(0, 16.51) * mm});
            skPoint(sketch, "E433", {"position": v(3.17, 18.03) * mm});
            skPoint(sketch, "E434", {"position": v(6.35, 21.59) * mm});
            skPoint(sketch, "E435", {"position": v(12.7, 27.43) * mm});
            skPoint(sketch, "E436", {"position": v(19.05, 32.26) * mm});
            skPoint(sketch, "E437", {"position": v(25.4, 36.32) * mm});
            skPoint(sketch, "E438", {"position": v(31.75, 39.12) * mm});
            skPoint(sketch, "E439", {"position": v(38.1, 44.07) * mm});
            skPoint(sketch, "E440", {"position": v(41.28, 47.88) * mm});
            skPoint(sketch, "E441", {"position": v(44.45, 54.36) * mm});
            skPoint(sketch, "E442", {"position": v(47.62, 64) * mm});
            skPoint(sketch, "E443", {"position": v(50.8, 75.44) * mm});
            skPoint(sketch, "E444", {"position": v(52.4, 93.22) * mm});
            skFitSpline(sketch, "E445", {"points": [v(52.4, 93.22) * mm, v(50.8, 75.44) * mm, v(47.62, 64) * mm, v(44.45, 54.36) * mm, v(41.28, 47.88) * mm, v(38.1, 44.07) * mm, v(31.75, 39.12) * mm, v(25.4, 36.32) * mm, v(19.05, 32.26) * mm, v(12.7, 27.43) * mm, v(6.35, 21.59) * mm, v(3.17, 18.03) * mm, v(0, 16.51) * mm], "startDerivative": vector(-6.87, -157.96) * mm, "endDerivative": vector(-80.78, 0.3) * mm});
            skFitSpline(sketch, "E446.MirrorCS", {"points": [v(-52.4, 93.22) * mm, v(-50.8, 75.44) * mm, v(-47.62, 64) * mm, v(-44.45, 54.36) * mm, v(-41.28, 47.88) * mm, v(-38.1, 44.07) * mm, v(-31.75, 39.12) * mm, v(-25.4, 36.32) * mm, v(-19.05, 32.26) * mm, v(-12.7, 27.43) * mm, v(-6.35, 21.59) * mm, v(-3.17, 18.03) * mm, v(0, 16.51) * mm], "startDerivative": vector(6.87, -157.96) * mm, "endDerivative": vector(80.78, 0.3) * mm});
            skSolve(sketch);
        }
        {
            var Q0;
            Q0=qCreatedBy(makeId("Front.planeOp"),FACE);
            cPlane(context, id + "F45", {"entities" : qUnion([Q0]), "cplaneType" : CPlaneType.OFFSET, "offset" : 1482.72 * mm, "width" : 152.4 * mm, "height" : 152.4 * mm});
        }
        {
            var Q0;
            Q0=qCreatedBy(id+"F45.planeOp",FACE);
            var sketch = newSketch(context, id + "F46", { "sketchPlane" : qUnion([Q0])});
            skPoint(sketch, "E447", {"position": v(0, 16.51) * mm});
            skPoint(sketch, "E448", {"position": v(3.17, 18.03) * mm});
            skPoint(sketch, "E449", {"position": v(6.35, 21.59) * mm});
            skPoint(sketch, "E450", {"position": v(12.7, 27.69) * mm});
            skPoint(sketch, "E451", {"position": v(19.05, 32.77) * mm});
            skPoint(sketch, "E452", {"position": v(25.4, 38.1) * mm});
            skPoint(sketch, "E453", {"position": v(31.75, 43.18) * mm});
            skPoint(sketch, "E454", {"position": v(38.1, 50.3) * mm});
            skPoint(sketch, "E455", {"position": v(41.27, 55.88) * mm});
            skPoint(sketch, "E456", {"position": v(44.45, 66.04) * mm});
            skPoint(sketch, "E457", {"position": v(47.62, 78.74) * mm});
            skPoint(sketch, "E458", {"position": v(49.23, 93.22) * mm});
            skFitSpline(sketch, "E459", {"points": [v(49.23, 93.22) * mm, v(47.62, 78.74) * mm, v(44.45, 66.04) * mm, v(41.28, 55.88) * mm, v(38.1, 50.3) * mm, v(31.75, 43.18) * mm, v(25.4, 38.1) * mm, v(19.05, 32.77) * mm, v(12.7, 27.69) * mm, v(6.35, 21.59) * mm, v(3.17, 18.03) * mm, v(0, 16.51) * mm], "startDerivative": vector(-8.66, -132.3) * mm, "endDerivative": vector(-66.43, -0.22) * mm});
            skFitSpline(sketch, "E460.MirrorCS", {"points": [v(-49.23, 93.22) * mm, v(-47.62, 78.74) * mm, v(-44.45, 66.04) * mm, v(-41.28, 55.88) * mm, v(-38.1, 50.3) * mm, v(-31.75, 43.18) * mm, v(-25.4, 38.1) * mm, v(-19.05, 32.77) * mm, v(-12.7, 27.69) * mm, v(-6.35, 21.59) * mm, v(-3.17, 18.03) * mm, v(0, 16.51) * mm], "startDerivative": vector(8.66, -132.3) * mm, "endDerivative": vector(66.43, -0.22) * mm});
            skSolve(sketch);
        }
        {
            var Q0;
            Q0=qCreatedBy(makeId("Top.planeOp"),FACE);
            cPlane(context, id + "F47", {"entities" : qUnion([Q0]), "cplaneType" : CPlaneType.OFFSET, "offset" : 93.22 * mm, "width" : 152.4 * mm, "height" : 152.4 * mm});
        }
        {
            var Q0;
            Q0=qCreatedBy(id+"F47.planeOp",FACE);
            var sketch = newSketch(context, id + "F48", { "sketchPlane" : qUnion([Q0])});
            skFitSpline(sketch, "E461", {"points": [v(-53.98, -296.88) * mm, v(-63.5, -371.48) * mm, v(-73.03, -444.5) * mm, v(-82.55, -517.52) * mm, v(-88.9, -590.55) * mm, v(-93.68, -658.83) * mm, v(-97.8, -730.25) * mm, v(-99.82, -801.7) * mm, v(-99.82, -874.73) * mm], "startDerivative": vector(2.88, -596.84) * mm, "endDerivative": vector(29.48, -593.05) * mm});
            skFitSpline(sketch, "E462", {"points": [v(-99.82, -874.73) * mm, v(-98.43, -949.33) * mm, v(-96.22, -1023.95) * mm, v(-91.44, -1096.98) * mm, v(-87.33, -1168.4) * mm, v(-82.55, -1233.5) * mm, v(-76.2, -1304.93) * mm, v(-66.68, -1377.95) * mm, v(-57.15, -1450.98) * mm, v(-52.4, -1463.67) * mm, v(-41.28, -1524) * mm, v(0, -1654.18) * mm], "startDerivative": vector(-18.42, -760.24) * mm, "endDerivative": vector(478.3, -4.41) * mm});
            skLineSegment(sketch, "E463", {"start": v(0, -1654.18) * mm, "end": v(0, -149.23) * mm});
            skFitSpline(sketch, "E464.MirrorCS", {"points": [v(53.98, -296.88) * mm, v(63.5, -371.48) * mm, v(73.03, -444.5) * mm, v(82.55, -517.52) * mm, v(88.9, -590.55) * mm, v(93.68, -658.83) * mm, v(97.8, -730.25) * mm, v(99.82, -801.7) * mm, v(99.82, -874.73) * mm], "startDerivative": vector(-2.88, -596.84) * mm, "endDerivative": vector(-29.48, -593.05) * mm});
            skFitSpline(sketch, "E465.MirrorCS", {"points": [v(99.82, -874.73) * mm, v(98.43, -949.33) * mm, v(96.22, -1023.95) * mm, v(91.44, -1096.98) * mm, v(87.33, -1168.4) * mm, v(82.55, -1233.5) * mm, v(76.2, -1304.93) * mm, v(66.68, -1377.95) * mm, v(57.15, -1450.98) * mm, v(52.4, -1463.67) * mm, v(41.28, -1524) * mm, v(0, -1654.18) * mm], "startDerivative": vector(18.42, -760.24) * mm, "endDerivative": vector(-478.3, -4.41) * mm});
            skSolve(sketch);
        }
        {
            var Q0;
            Q0=sQuery(id+"F48.wireOp",EDGE,"E462");
            var Q1;
            Q1=sQuery(id+"F48.wireOp",EDGE,"E465.MirrorCS");
            loft(context, id + "F49", {"bodyType" : ToolBodyType.SURFACE, "wireProfilesArray" : [{ "wireProfileEntities" : qUnion([Q0]) }, { "wireProfileEntities" : qUnion([Q1]) }]});
        }
        {
            var Q0;
            Q0=sQuery(id+"F48.wireOp",EDGE,"E461");
            var Q1;
            Q1=sQuery(id+"F48.wireOp",EDGE,"E464.MirrorCS");
            loft(context, id + "F50", {"bodyType" : ToolBodyType.SURFACE, "wireProfilesArray" : [{ "wireProfileEntities" : qUnion([Q0]) }, { "wireProfileEntities" : qUnion([Q1]) }]});
        }
    });
